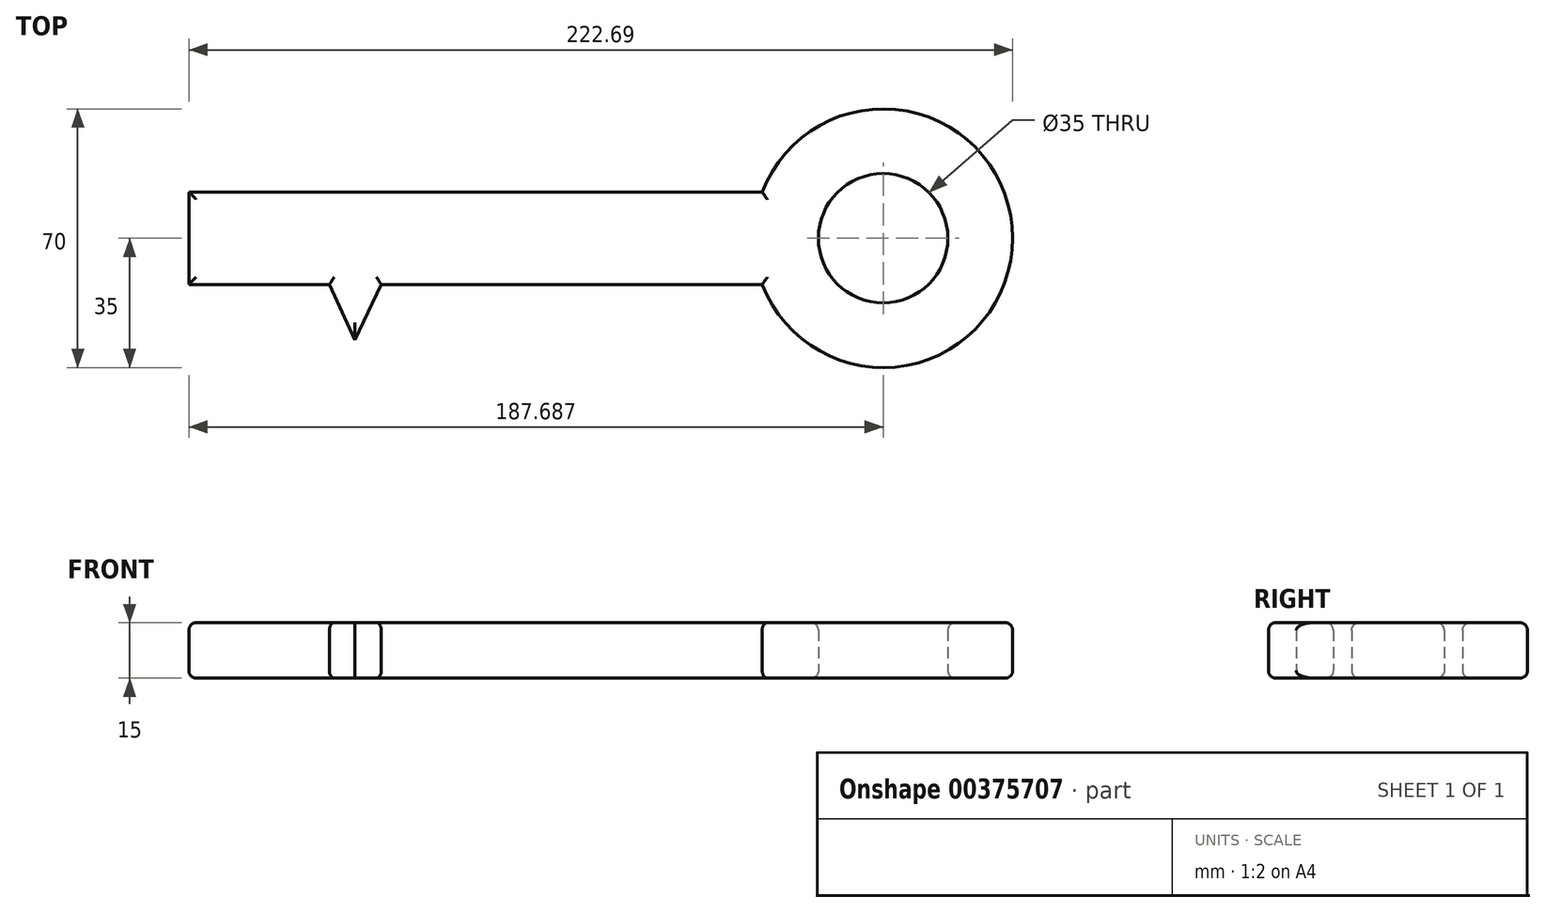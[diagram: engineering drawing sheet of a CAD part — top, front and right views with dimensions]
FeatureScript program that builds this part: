
annotation { "Feature Type Name" : "Feature", "Feature Type Description" : "" }
export const myFeature = defineFeature(function(context is Context, id is Id, definition is map)
    precondition{}
    {
        {
            var Q0;
            Q0=qCreatedBy(makeId("Top.planeOp"),FACE);
            var sketch = newSketch(context, id + "F0", { "sketchPlane" : qUnion([Q0])});
            skLineSegment(sketch, "E0.bottom", {"start": v(-21.33, 12.5) * mm, "end": v(-176.33, 12.5) * mm});
            skLineSegment(sketch, "E0.top", {"start": v(-21.33, -12.5) * mm, "end": v(-176.33, -12.5) * mm});
            skLineSegment(sketch, "E0.left", {"start": v(-21.33, 12.5) * mm, "end": v(-21.33, -12.5) * mm});
            skLineSegment(sketch, "E0.right", {"start": v(-176.33, 12.5) * mm, "end": v(-176.33, -12.5) * mm});
            skLineSegment(sketch, "E1.bottom", {"start": v(-176.33, -12.5) * mm, "end": v(-166.33, -12.5) * mm});
            skLineSegment(sketch, "E1.top", {"start": v(-176.33, -42.5) * mm, "end": v(-166.33, -42.5) * mm});
            skLineSegment(sketch, "E1.left", {"start": v(-176.33, -12.5) * mm, "end": v(-176.33, -42.5) * mm});
            skLineSegment(sketch, "E1.right", {"start": v(-166.33, -12.5) * mm, "end": v(-166.33, -42.5) * mm});
            skLineSegment(sketch, "E2.bottom", {"start": v(-148.33, -12.5) * mm, "end": v(-156.33, -12.5) * mm});
            skLineSegment(sketch, "E2.top", {"start": v(-148.33, -27.5) * mm, "end": v(-156.33, -27.5) * mm});
            skLineSegment(sketch, "E2.left", {"start": v(-148.33, -12.5) * mm, "end": v(-148.33, -27.5) * mm});
            skLineSegment(sketch, "E2.right", {"start": v(-156.33, -12.5) * mm, "end": v(-156.33, -27.5) * mm});
            skLineSegment(sketch, "E3", {"start": v(-138.33, -12.5) * mm, "end": v(-131.42, -27.5) * mm});
            skLineSegment(sketch, "E4", {"start": v(-131.42, -27.5) * mm, "end": v(-124.33, -12.5) * mm});
            skArc(sketch, "E5", {"start": v(-21.33, -12.5) * mm, "mid": v(46.36, 0) * mm, "end": v(-21.33, 12.5) * mm});
            skCircle(sketch, "E6", {"center": v(11.36, 0) * mm, "radius": 17.5 * mm});
            skLineSegment(sketch, "E7", {"start": v(11.36, 0) * mm, "end": v(-176.33, 0) * mm, "construction": true});
            skSolve(sketch);
        }
        {
            var Q0;
            Q0=makeQuery(id+"F0.imprint","IMPRINT",FACE,{"disambiguationData":[TD([[makeQuery(id+"F0.imprint","IMPRINT",EDGE,{"derivedFrom":sQuery(id+"F0.wireOp",EDGE,"E0.bottom")}),1.0]])]});
            var Q1;
            Q1=makeQuery(id+"F0.imprint","IMPRINT",FACE,{"disambiguationData":[TD([[makeQuery(id+"F0.imprint","IMPRINT",EDGE,{"derivedFrom":sQuery(id+"F0.wireOp",EDGE,"E2.bottom")}),1.0]])]});
            var Q2;
            Q2=makeQuery(id+"F0.imprint","IMPRINT",FACE,{"disambiguationData":[TD([[makeQuery(id+"F0.imprint","IMPRINT",EDGE,{"derivedFrom":sQuery(id+"F0.wireOp",EDGE,"E1.bottom")}),-1.0]])]});
            var Q3;
            {var subQ0=sQuery(id+"F0.wireOp",EDGE,"E3");Q3=makeQuery(id+"F0.imprint","IMPRINT",FACE,{"disambiguationData":[TD([[makeQuery(id+"F0.imprint","IMPRINT",EDGE,{"derivedFrom":subQ0}),1.0]])]});}
            var Q4;
            Q4=makeQuery(id+"F0.imprint","IMPRINT",FACE,{"disambiguationData":[TD([[makeQuery(id+"F0.imprint","IMPRINT",EDGE,{"derivedFrom":sQuery(id+"F0.wireOp",EDGE,"E0.left")}),1.0]])]});
            extrude(context, id + "F1", {"entities" : qUnion([Q0, Q1, Q2, Q3, Q4]), "depth" : 15 * mm});
        }
        {
            var Q0;
            Q0=makeQuery(id+"F1.opExtrude","CAP_EDGE",EDGE,{"disambiguationData":[OSD([sQuery(id+"F0.wireOp",EDGE,"E0.bottom")])],"isStart":false});
            var Q1;
            {var subQ0=sQuery(id+"F0.wireOp",EDGE,"E0.top");Q1=makeQuery(id+"F1.opExtrude","CAP_EDGE",EDGE,{"disambiguationData":[OSD([subQ0]),TDD([makeQuery(id+"F0.imprint","IMPRINT",EDGE,{"disambiguationData":[TD([[makeQuery(id+"F0.imprint","INTERSECT",VERTEX,{"derivedFrom":[subQ0,sQuery(id+"F0.wireOp",EDGE,"E4")]}),1.0]])],"derivedFrom":subQ0})])],"isStart":false});}
            var Q2;
            Q2=makeQuery(id+"F1.opExtrude","CAP_EDGE",EDGE,{"disambiguationData":[OSD([sQuery(id+"F0.wireOp",EDGE,"E4")])],"isStart":false});
            var Q3;
            Q3=makeQuery(id+"F1.opExtrude","CAP_EDGE",EDGE,{"disambiguationData":[OSD([sQuery(id+"F0.wireOp",EDGE,"E3")])],"isStart":false});
            var Q4;
            Q4=makeQuery(id+"F1.opExtrude","CAP_EDGE",EDGE,{"disambiguationData":[OSD([sQuery(id+"F0.wireOp",EDGE,"E2.left")])],"isStart":false});
            var Q5;
            {var subQ0=sQuery(id+"F0.wireOp",EDGE,"E0.top");Q5=makeQuery(id+"F1.opExtrude","CAP_EDGE",EDGE,{"disambiguationData":[OSD([subQ0]),TDD([makeQuery(id+"F0.imprint","IMPRINT",EDGE,{"disambiguationData":[TD([[makeQuery(id+"F0.imprint","INTERSECT",VERTEX,{"derivedFrom":[subQ0,sQuery(id+"F0.wireOp",EDGE,"E3")]}),-1.0]])],"derivedFrom":subQ0})])],"isStart":false});}
            var Q6;
            {var subQ0=sQuery(id+"F0.wireOp",EDGE,"E0.top");Q6=makeQuery(id+"F1.opExtrude","CAP_EDGE",EDGE,{"disambiguationData":[OSD([subQ0]),TDD([makeQuery(id+"F0.imprint","IMPRINT",EDGE,{"disambiguationData":[TD([[makeQuery(id+"F0.imprint","INTERSECT",VERTEX,{"derivedFrom":[subQ0,sQuery(id+"F0.wireOp",EDGE,"E1.bottom"),sQuery(id+"F0.wireOp",EDGE,"E1.right")]}),1.0]])],"derivedFrom":subQ0})])],"isStart":false});}
            var Q7;
            Q7=makeQuery(id+"F1.opExtrude","CAP_EDGE",EDGE,{"disambiguationData":[OSD([sQuery(id+"F0.wireOp",EDGE,"E1.right")])],"isStart":false});
            var Q8;
            Q8=makeQuery(id+"F1.opExtrude","CAP_EDGE",EDGE,{"disambiguationData":[OSD([sQuery(id+"F0.wireOp",EDGE,"E1.top")])],"isStart":false});
            var Q9;
            Q9=makeQuery(id+"F1.opExtrude","CAP_EDGE",EDGE,{"disambiguationData":[OSD([sQuery(id+"F0.wireOp",EDGE,"E0.right"),sQuery(id+"F0.wireOp",EDGE,"E1.left")])],"isStart":false});
            var Q10;
            Q10=makeQuery(id+"F1.opExtrude","CAP_EDGE",EDGE,{"disambiguationData":[OSD([sQuery(id+"F0.wireOp",EDGE,"E5")])],"isStart":false});
            var Q11;
            Q11=makeQuery(id+"F1.opExtrude","CAP_EDGE",EDGE,{"disambiguationData":[OSD([sQuery(id+"F0.wireOp",EDGE,"E6")])],"isStart":false});
            var Q12;
            Q12=makeQuery(id+"F1.opExtrude","CAP_EDGE",EDGE,{"disambiguationData":[OSD([sQuery(id+"F0.wireOp",EDGE,"E0.bottom")])],"isStart":true});
            var Q13;
            {var subQ0=sQuery(id+"F0.wireOp",EDGE,"E0.top");Q13=makeQuery(id+"F1.opExtrude","CAP_EDGE",EDGE,{"disambiguationData":[OSD([subQ0]),TDD([makeQuery(id+"F0.imprint","IMPRINT",EDGE,{"disambiguationData":[TD([[makeQuery(id+"F0.imprint","INTERSECT",VERTEX,{"derivedFrom":[subQ0,sQuery(id+"F0.wireOp",EDGE,"E4")]}),1.0]])],"derivedFrom":subQ0})])],"isStart":true});}
            var Q14;
            Q14=makeQuery(id+"F1.opExtrude","CAP_EDGE",EDGE,{"disambiguationData":[OSD([sQuery(id+"F0.wireOp",EDGE,"E4")])],"isStart":true});
            var Q15;
            {var subQ0=sQuery(id+"F0.wireOp",EDGE,"E0.top");Q15=makeQuery(id+"F1.opExtrude","CAP_EDGE",EDGE,{"disambiguationData":[OSD([subQ0]),TDD([makeQuery(id+"F0.imprint","IMPRINT",EDGE,{"disambiguationData":[TD([[makeQuery(id+"F0.imprint","INTERSECT",VERTEX,{"derivedFrom":[subQ0,sQuery(id+"F0.wireOp",EDGE,"E3")]}),-1.0]])],"derivedFrom":subQ0})])],"isStart":true});}
            var Q16;
            Q16=makeQuery(id+"F1.opExtrude","CAP_EDGE",EDGE,{"disambiguationData":[OSD([sQuery(id+"F0.wireOp",EDGE,"E3")])],"isStart":true});
            var Q17;
            Q17=makeQuery(id+"F1.opExtrude","CAP_EDGE",EDGE,{"disambiguationData":[OSD([sQuery(id+"F0.wireOp",EDGE,"E2.left")])],"isStart":true});
            var Q18;
            Q18=makeQuery(id+"F1.opExtrude","CAP_EDGE",EDGE,{"disambiguationData":[OSD([sQuery(id+"F0.wireOp",EDGE,"E5")])],"isStart":true});
            var Q19;
            Q19=makeQuery(id+"F1.opExtrude","CAP_EDGE",EDGE,{"disambiguationData":[OSD([sQuery(id+"F0.wireOp",EDGE,"E6")])],"isStart":true});
            var Q20;
            Q20=makeQuery(id+"F1.opExtrude","CAP_EDGE",EDGE,{"disambiguationData":[OSD([sQuery(id+"F0.wireOp",EDGE,"E0.right"),sQuery(id+"F0.wireOp",EDGE,"E1.left")])],"isStart":true});
            var Q21;
            Q21=makeQuery(id+"F1.opExtrude","CAP_EDGE",EDGE,{"disambiguationData":[OSD([sQuery(id+"F0.wireOp",EDGE,"E1.right")])],"isStart":true});
            var Q22;
            {var subQ0=sQuery(id+"F0.wireOp",EDGE,"E0.top");Q22=makeQuery(id+"F1.opExtrude","CAP_EDGE",EDGE,{"disambiguationData":[OSD([subQ0]),TDD([makeQuery(id+"F0.imprint","IMPRINT",EDGE,{"disambiguationData":[TD([[makeQuery(id+"F0.imprint","INTERSECT",VERTEX,{"derivedFrom":[subQ0,sQuery(id+"F0.wireOp",EDGE,"E1.bottom"),sQuery(id+"F0.wireOp",EDGE,"E1.right")]}),1.0]])],"derivedFrom":subQ0})])],"isStart":true});}
            fillet(context, id + "F2", {"entities" : qUnion([Q0, Q1, Q2, Q3, Q4, Q5, Q6, Q7, Q8, Q9, Q10, Q11, Q12, Q13, Q14, Q15, Q16, Q17, Q18, Q19, Q20, Q21, Q22]), "radius" : 2 * mm, "tangentPropagation" : true, "allowEdgeOverflow" : false});
        }
    });
